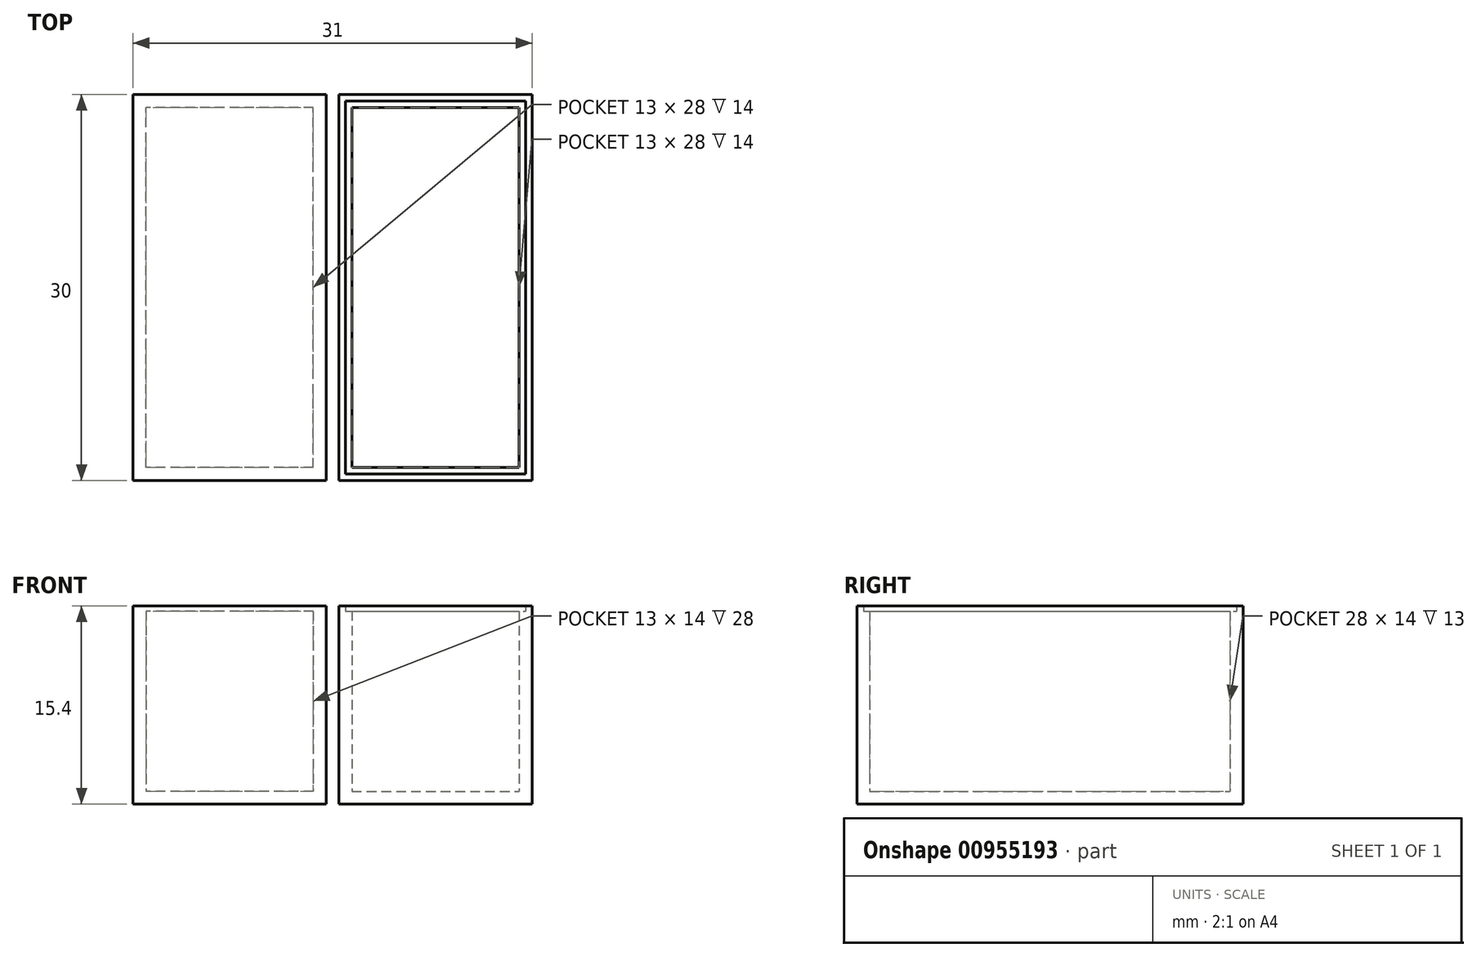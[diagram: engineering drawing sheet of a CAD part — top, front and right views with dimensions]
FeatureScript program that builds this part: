
annotation { "Feature Type Name" : "Feature", "Feature Type Description" : "" }
export const myFeature = defineFeature(function(context is Context, id is Id, definition is map)
    precondition{}
    {
        {
            var Q0;
            Q0=qCreatedBy(makeId("Front.planeOp"),FACE);
            var sketch = newSketch(context, id + "F0", { "sketchPlane" : qUnion([Q0])});
            skLineSegment(sketch, "E0.bottom", {"start": v(1, 15) * mm, "end": v(16, 15) * mm});
            skLineSegment(sketch, "E0.top", {"start": v(1, 0) * mm, "end": v(16, 0) * mm});
            skLineSegment(sketch, "E0.left", {"start": v(1, 15) * mm, "end": v(1, 0) * mm});
            skLineSegment(sketch, "E0.right", {"start": v(16, 15) * mm, "end": v(16, 0) * mm});
            skLineSegment(sketch, "E1.bottom", {"start": v(0, 15) * mm, "end": v(-15, 15) * mm});
            skLineSegment(sketch, "E1.top", {"start": v(0, 0) * mm, "end": v(-15, 0) * mm});
            skLineSegment(sketch, "E1.left", {"start": v(0, 15) * mm, "end": v(0, 0) * mm});
            skLineSegment(sketch, "E1.right", {"start": v(-15, 15) * mm, "end": v(-15, 0) * mm});
            skSolve(sketch);
        }
        {
            var Q0;
            Q0=makeQuery(id+"F0.imprint","IMPRINT",FACE,{"disambiguationData":[TD([[makeQuery(id+"F0.imprint","IMPRINT",EDGE,{"derivedFrom":sQuery(id+"F0.wireOp",EDGE,"E0.bottom")}),-1.0]])]});
            extrude(context, id + "F1", {"entities" : qUnion([Q0]), "endBound" : BoundingType.SYMMETRIC, "depth" : 30 * mm, "offsetDistance" : 25 * mm});
        }
        {
            var Q0;
            Q0=makeQuery(id+"F0.imprint","IMPRINT",FACE,{"disambiguationData":[TD([[makeQuery(id+"F0.imprint","IMPRINT",EDGE,{"derivedFrom":sQuery(id+"F0.wireOp",EDGE,"E1.bottom")}),1.0]])]});
            extrude(context, id + "F2", {"entities" : qUnion([Q0]), "endBound" : BoundingType.SYMMETRIC, "depth" : 30 * mm, "offsetDistance" : 25 * mm});
        }
        {
            var Q0;
            Q0=qCreatedBy(makeId("Front.planeOp"),FACE);
            var sketch = newSketch(context, id + "F3", { "sketchPlane" : qUnion([Q0])});
            skLineSegment(sketch, "E2", {"start": v(0, 0) * mm, "end": v(0, 15) * mm});
            skLineSegment(sketch, "E3", {"start": v(0, 15) * mm, "end": v(-2, 15) * mm});
            skLineSegment(sketch, "E4", {"start": v(-2, 15) * mm, "end": v(0, 0) * mm});
            skLineSegment(sketch, "E5", {"start": v(1, 0) * mm, "end": v(1, 15) * mm});
            skLineSegment(sketch, "E6", {"start": v(1, 15) * mm, "end": v(3, 15) * mm});
            skLineSegment(sketch, "E7", {"start": v(3, 15) * mm, "end": v(1, 0) * mm});
            skLineSegment(sketch, "E8.bottom", {"start": v(0, 15) * mm, "end": v(-15, 15) * mm});
            skLineSegment(sketch, "E8.top", {"start": v(0, 15.4) * mm, "end": v(-15, 15.4) * mm});
            skLineSegment(sketch, "E8.left", {"start": v(0, 15) * mm, "end": v(0, 15.4) * mm});
            skLineSegment(sketch, "E8.right", {"start": v(-15, 15) * mm, "end": v(-15, 15.4) * mm});
            skLineSegment(sketch, "E9.bottom", {"start": v(1, 15) * mm, "end": v(16, 15) * mm});
            skLineSegment(sketch, "E9.top", {"start": v(1, 15.4) * mm, "end": v(16, 15.4) * mm});
            skLineSegment(sketch, "E9.left", {"start": v(1, 15) * mm, "end": v(1, 15.4) * mm});
            skLineSegment(sketch, "E9.right", {"start": v(16, 15) * mm, "end": v(16, 15.4) * mm});
            skArc(sketch, "E10", {"start": v(1, 15.4) * mm, "mid": v(0.5, 15.9) * mm, "end": v(0, 15.4) * mm});
            skArc(sketch, "E11.0", {"start": v(1.5, 15.4) * mm, "mid": v(0.5, 16.4) * mm, "end": v(-0.5, 15.4) * mm});
            skLineSegment(sketch, "E12.bottom", {"start": v(1.5, 15.4) * mm, "end": v(15.5, 15.4) * mm});
            skLineSegment(sketch, "E12.top", {"start": v(1.5, 15) * mm, "end": v(15.5, 15) * mm});
            skLineSegment(sketch, "E12.left", {"start": v(1.5, 15.4) * mm, "end": v(1.5, 15) * mm});
            skLineSegment(sketch, "E12.right", {"start": v(15.5, 15.4) * mm, "end": v(15.5, 15) * mm});
            skLineSegment(sketch, "E13.bottom", {"start": v(-0.5, 15.4) * mm, "end": v(-14.5, 15.4) * mm});
            skLineSegment(sketch, "E13.top", {"start": v(-0.5, 15) * mm, "end": v(-14.5, 15) * mm});
            skLineSegment(sketch, "E13.left", {"start": v(-0.5, 15.4) * mm, "end": v(-0.5, 15) * mm});
            skLineSegment(sketch, "E13.right", {"start": v(-14.5, 15.4) * mm, "end": v(-14.5, 15) * mm});
            skSolve(sketch);
        }
        {
            var Q0;
            Q0=makeQuery(id+"F1.opExtrude","SWEPT_FACE",FACE,{"disambiguationData":[OSD([sQuery(id+"F0.wireOp",EDGE,"E0.bottom")])]});
            shell(context, id + "F4", {"entities" : qUnion([Q0]), "thickness" : 1 * mm});
        }
        {
            var Q0;
            Q0=makeQuery(id+"F2.opExtrude","SWEPT_FACE",FACE,{"disambiguationData":[OSD([sQuery(id+"F0.wireOp",EDGE,"E1.bottom")])]});
            shell(context, id + "F5", {"entities" : qUnion([Q0]), "thickness" : 1 * mm});
        }
        {
            var Q0;
            {var subQ0=sQuery(id+"F3.wireOp",EDGE,"E9.left");Q0=makeQuery(id+"F3.imprint","IMPRINT",FACE,{"disambiguationData":[TD([[makeQuery(id+"F3.imprint","IMPRINT",EDGE,{"derivedFrom":subQ0}),-1.0]])]});}
            var Q1;
            {var subQ0=sQuery(id+"F3.wireOp",EDGE,"E9.right");Q1=makeQuery(id+"F3.imprint","IMPRINT",FACE,{"disambiguationData":[TD([[makeQuery(id+"F3.imprint","IMPRINT",EDGE,{"derivedFrom":subQ0}),1.0]])]});}
            var Q2;
            {var subQ0=sQuery(id+"F3.wireOp",EDGE,"E8.left");Q2=makeQuery(id+"F3.imprint","IMPRINT",FACE,{"disambiguationData":[TD([[makeQuery(id+"F3.imprint","IMPRINT",EDGE,{"derivedFrom":subQ0}),1.0]])]});}
            var Q3;
            {var subQ0=sQuery(id+"F3.wireOp",EDGE,"E8.right");Q3=makeQuery(id+"F3.imprint","IMPRINT",FACE,{"disambiguationData":[TD([[makeQuery(id+"F3.imprint","IMPRINT",EDGE,{"derivedFrom":subQ0}),-1.0]])]});}
            var Q4;
            {var subQ0=sQuery(id+"F3.wireOp",EDGE,"E13.left");Q4=makeQuery(id+"F3.imprint","IMPRINT",FACE,{"disambiguationData":[TD([[makeQuery(id+"F3.imprint","IMPRINT",EDGE,{"derivedFrom":subQ0}),-1.0]])]});}
            var Q5;
            {var subQ0=sQuery(id+"F3.wireOp",EDGE,"E12.left");Q5=makeQuery(id+"F3.imprint","IMPRINT",FACE,{"disambiguationData":[TD([[makeQuery(id+"F3.imprint","IMPRINT",EDGE,{"derivedFrom":subQ0}),1.0]])]});}
            extrude(context, id + "F6", {"entities" : qUnion([Q0, Q1, Q2, Q3, Q4, Q5]), "operationType" : NewBodyOperationType.ADD, "endBound" : BoundingType.SYMMETRIC, "depth" : 30 * mm, "offsetDistance" : 25 * mm});
        }
        {
            var Q0;
            {var subQ0=sQuery(id+"F3.wireOp",EDGE,"E12.left");Q0=makeQuery(id+"F3.imprint","IMPRINT",FACE,{"disambiguationData":[TD([[makeQuery(id+"F3.imprint","IMPRINT",EDGE,{"derivedFrom":subQ0}),1.0]])]});}
            extrude(context, id + "F7", {"entities" : qUnion([Q0]), "operationType" : NewBodyOperationType.REMOVE, "endBound" : BoundingType.SYMMETRIC, "depth" : 29 * mm, "offsetDistance" : 25 * mm});
        }
    });
